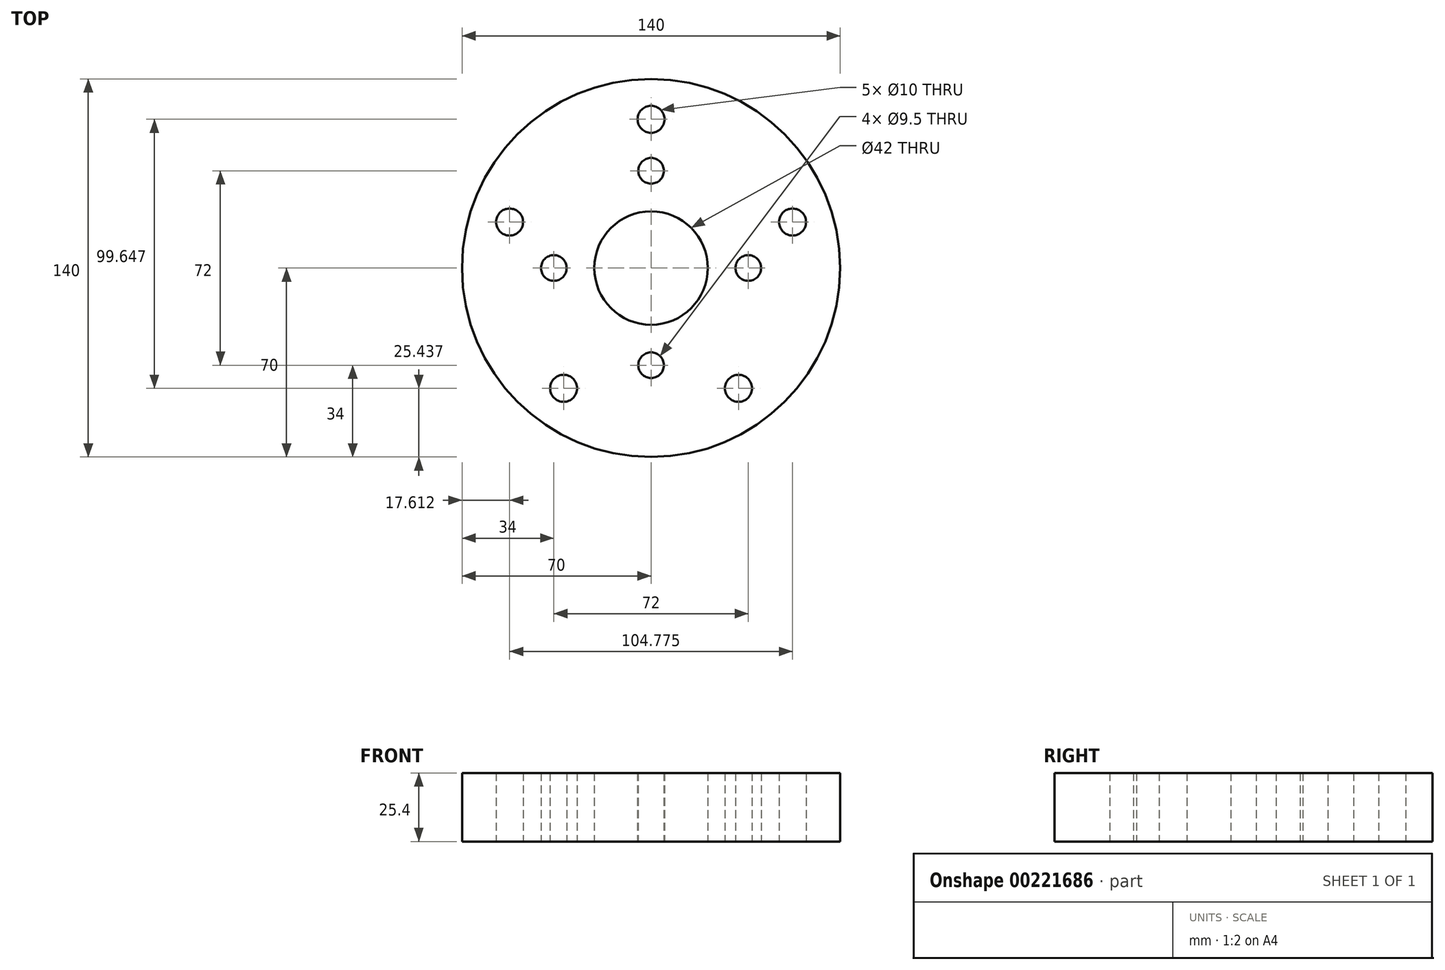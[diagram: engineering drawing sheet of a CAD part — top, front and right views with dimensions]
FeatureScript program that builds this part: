
annotation { "Feature Type Name" : "Feature", "Feature Type Description" : "" }
export const myFeature = defineFeature(function(context is Context, id is Id, definition is map)
    precondition{}
    {
        {
            var Q0;
            Q0=qCreatedBy(makeId("Top.planeOp"),FACE);
            var sketch = newSketch(context, id + "F0", { "sketchPlane" : qUnion([Q0])});
            skCircle(sketch, "E0", {"center": v(0, 55.08) * mm, "radius": 5 * mm});
            skCircle(sketch, "E1.1.0", {"center": v(-52.39, 17.02) * mm, "radius": 5 * mm});
            skCircle(sketch, "E1.2.0", {"center": v(-32.38, -44.56) * mm, "radius": 5 * mm});
            skCircle(sketch, "E1.3.0", {"center": v(32.38, -44.56) * mm, "radius": 5 * mm});
            skCircle(sketch, "E1.4.0", {"center": v(52.39, 17.02) * mm, "radius": 5 * mm});
            skPoint(sketch, "E1.center", {"position": v(0, 0) * mm});
            skCircle(sketch, "E2", {"center": v(0, 0) * mm, "radius": 70 * mm});
            skCircle(sketch, "E3", {"center": v(0, 0) * mm, "radius": 21 * mm});
            skCircle(sketch, "E4", {"center": v(0, 36) * mm, "radius": 4.75 * mm});
            skCircle(sketch, "E5.1.0", {"center": v(-36, 0) * mm, "radius": 4.75 * mm});
            skCircle(sketch, "E5.2.0", {"center": v(0, -36) * mm, "radius": 4.75 * mm});
            skCircle(sketch, "E5.3.0", {"center": v(36, 0) * mm, "radius": 4.75 * mm});
            skSolve(sketch);
        }
        {
            var Q0;
            Q0=qSketchRegion(id+"F0",true);
            extrude(context, id + "F1", {"entities" : qUnion([Q0]), "depth" : 25.4 * mm});
        }
    });
